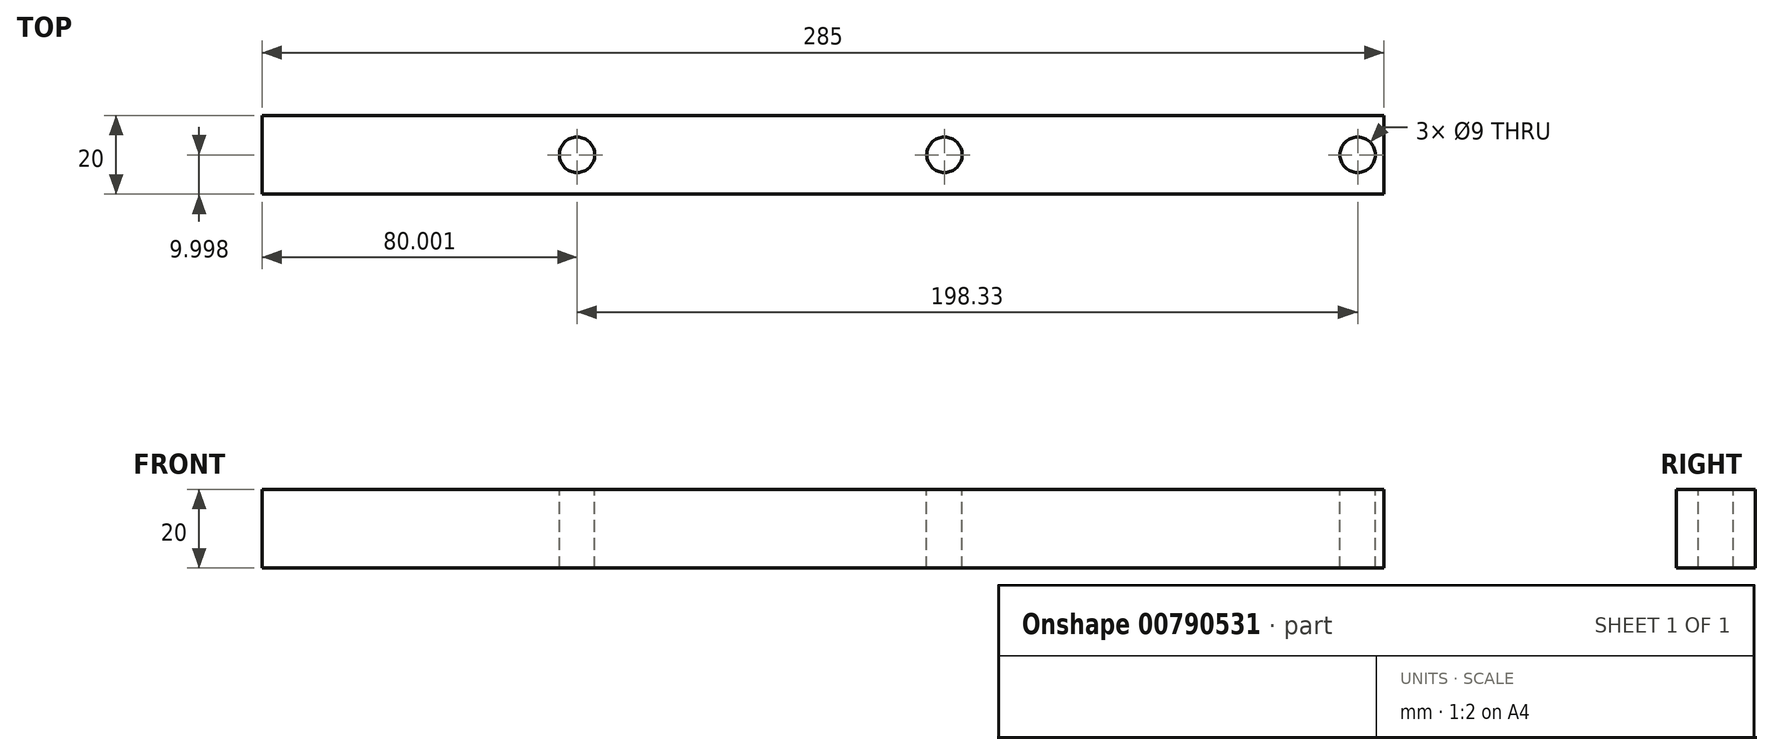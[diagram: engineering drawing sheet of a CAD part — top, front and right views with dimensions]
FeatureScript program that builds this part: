
annotation { "Feature Type Name" : "Feature", "Feature Type Description" : "" }
export const myFeature = defineFeature(function(context is Context, id is Id, definition is map)
    precondition{}
    {
        {
            var Q0;
            Q0=qCreatedBy(makeId("Top.planeOp"),FACE);
            var sketch = newSketch(context, id + "F0", { "sketchPlane" : qUnion([Q0])});
            skLineSegment(sketch, "E0.bottom", {"start": v(-325.16, -21.54) * mm, "end": v(324.84, -21.54) * mm});
            skLineSegment(sketch, "E0.top", {"start": v(-325.16, -41.54) * mm, "end": v(324.84, -41.54) * mm});
            skLineSegment(sketch, "E0.left", {"start": v(-325.16, -21.54) * mm, "end": v(-325.16, -41.54) * mm});
            skLineSegment(sketch, "E0.right", {"start": v(324.84, -21.54) * mm, "end": v(324.84, -41.54) * mm});
            skSolve(sketch);
        }
        {
            var Q0;
            Q0=makeQuery(id+"F0.imprint","IMPRINT",FACE,{"disambiguationData":[TD([[makeQuery(id+"F0.imprint","IMPRINT",EDGE,{"derivedFrom":sQuery(id+"F0.wireOp",EDGE,"E0.bottom")}),-1.0]])]});
            extrude(context, id + "F1", {"entities" : qUnion([Q0]), "depth" : 20 * mm, "offsetDistance" : 25 * mm});
        }
        {
            var Q0;
            Q0=makeQuery(id+"F1.opExtrude","CAP_FACE",FACE,{"disambiguationData":[OSD([sQuery(id+"F0.wireOp",EDGE,"E0.bottom"),sQuery(id+"F0.wireOp",EDGE,"E0.top"),sQuery(id+"F0.wireOp",EDGE,"E0.left"),sQuery(id+"F0.wireOp",EDGE,"E0.right")])],"isStart":false});
            var sketch = newSketch(context, id + "F2", { "sketchPlane" : qUnion([Q0])});
            skLineSegment(sketch, "E1", {"start": v(-325.16, -31.54) * mm, "end": v(-245.16, -31.54) * mm});
            skLineSegment(sketch, "E2", {"start": v(-245.16, -31.54) * mm, "end": v(-151.82, -31.54) * mm});
            skLineSegment(sketch, "E3", {"start": v(-151.82, -31.54) * mm, "end": v(-0.16, -31.54) * mm});
            skLineSegment(sketch, "E4", {"start": v(-0.16, -31.54) * mm, "end": v(46.51, -31.54) * mm});
            skLineSegment(sketch, "E5", {"start": v(-0.16, -31.54) * mm, "end": v(-46.83, -31.54) * mm});
            skPoint(sketch, "E6", {"position": v(-245.16, -31.54) * mm});
            skPoint(sketch, "E7", {"position": v(-151.82, -31.54) * mm});
            skPoint(sketch, "E8", {"position": v(-46.83, -31.54) * mm});
            skPoint(sketch, "E9", {"position": v(46.51, -31.54) * mm});
            skSolve(sketch);
        }
        {
            var Q0;
            Q0=sQuery(id+"F2.wireOp",VERTEX,"E6");
            var Q1;
            Q1=sQuery(id+"F2.wireOp",VERTEX,"E7");
            var Q2;
            Q2=sQuery(id+"F2.wireOp",VERTEX,"E8");
            var Q3;
            Q3=sQuery(id+"F2.wireOp",VERTEX,"E9");
            var Q4;
            Q4=makeQuery(id+"F1.opExtrude","SWEPT_BODY",BODY,{"disambiguationData":[OSD([sQuery(id+"F0.wireOp",EDGE,"E0.bottom"),sQuery(id+"F0.wireOp",EDGE,"E0.top"),sQuery(id+"F0.wireOp",EDGE,"E0.left"),sQuery(id+"F0.wireOp",EDGE,"E0.right")])]});
            hole(context, id + "F3", {"style" : HoleStyle.SIMPLE, "endStyle" : HoleEndStyle.THROUGH, "holeDiameter" : 9 * mm, "majorDiameter" : 5 * mm, "isTappedThrough" : true, "tappedDepth" : 12 * mm, "tapClearance" : 3, "locations" : qUnion([Q0, Q1, Q2, Q3]), "scope" : qUnion([Q4])});
        }
        {
            var Q0;
            Q0=makeQuery(id+"F1.opExtrude","CAP_FACE",FACE,{"disambiguationData":[OSD([sQuery(id+"F0.wireOp",EDGE,"E0.bottom"),sQuery(id+"F0.wireOp",EDGE,"E0.top"),sQuery(id+"F0.wireOp",EDGE,"E0.left"),sQuery(id+"F0.wireOp",EDGE,"E0.right")])],"isStart":false});
            var sketch = newSketch(context, id + "F4", { "sketchPlane" : qUnion([Q0])});
            skLineSegment(sketch, "E10", {"start": v(-325.16, -31.54) * mm, "end": v(-40.16, -31.54) * mm, "construction": true});
            skLineSegment(sketch, "E11.bottom", {"start": v(-40.16, -10.86) * mm, "end": v(360.22, -10.86) * mm});
            skLineSegment(sketch, "E11.top", {"start": v(-40.16, -54.84) * mm, "end": v(360.22, -54.84) * mm});
            skLineSegment(sketch, "E11.left", {"start": v(-40.16, -10.86) * mm, "end": v(-40.16, -54.84) * mm});
            skLineSegment(sketch, "E11.right", {"start": v(360.22, -10.86) * mm, "end": v(360.22, -54.84) * mm});
            skSolve(sketch);
        }
        {
            var Q0;
            {var subQ0=makeQuery(id+"F1.opExtrude","CAP_EDGE",EDGE,{"disambiguationData":[OSD([sQuery(id+"F0.wireOp",EDGE,"E0.right")])],"isStart":false});Q0=makeQuery(id+"F4.imprint","IMPRINT",FACE,{"disambiguationData":[TD([[makeQuery(id+"F4.imprint","IMPRINT",EDGE,{"derivedFrom":subQ0}),-1.0]])]});}
            extrude(context, id + "F5", {"entities" : qUnion([Q0]), "operationType" : NewBodyOperationType.REMOVE, "oppositeDirection" : true, "depth" : 25 * mm, "offsetDistance" : 25 * mm});
        }
    });
